# Revit family: QF_Vollrath 71001
name_source: partatom
category: Specialty Equipment
revit_build: Autodesk Revit 2016 (Build: 20151007_0715(x64)
units: mm (PartAtom-declared; Revit-internal decimal feet)

## family parameters
Always vertical = Yes
Cut with Voids When Loaded = No
OmniClass Number = 23.40.40.11.31
OmniClass Title = Steam Tables
Part Type = Normal
Room Calculation Point = No
Round Connector Dimension = Use Diameter
Shared = No
Work Plane-Based = No

## types (1)
- 71001
    Apparent Power = 696 VA
    Assembly Code = E1090320
    CSI MasterFormat = 11 42 13
    Conn Plug = NEMA 5-20P
    Cycle = 60 Hz
    Depth = 21.75 "
    Description = Warmer, Food Electric
    Elec Conn Connection Height = 2 "
    FL Amps = 6 A
    Height = 9 "
    Leg Height = 1 "
    Manufacturer = Vollrath
    Model = 71001
    Phase = 1
    URL = www.vollrathco.com
    Volts = 120 V
    Watts = 700 W
    Weight in Pounds = 19.85
    Width = 13.75 "

## geometry (parser evidence)
native form markers: Blend x27, Sweep x3
no freeform markers — native parametric forms only
